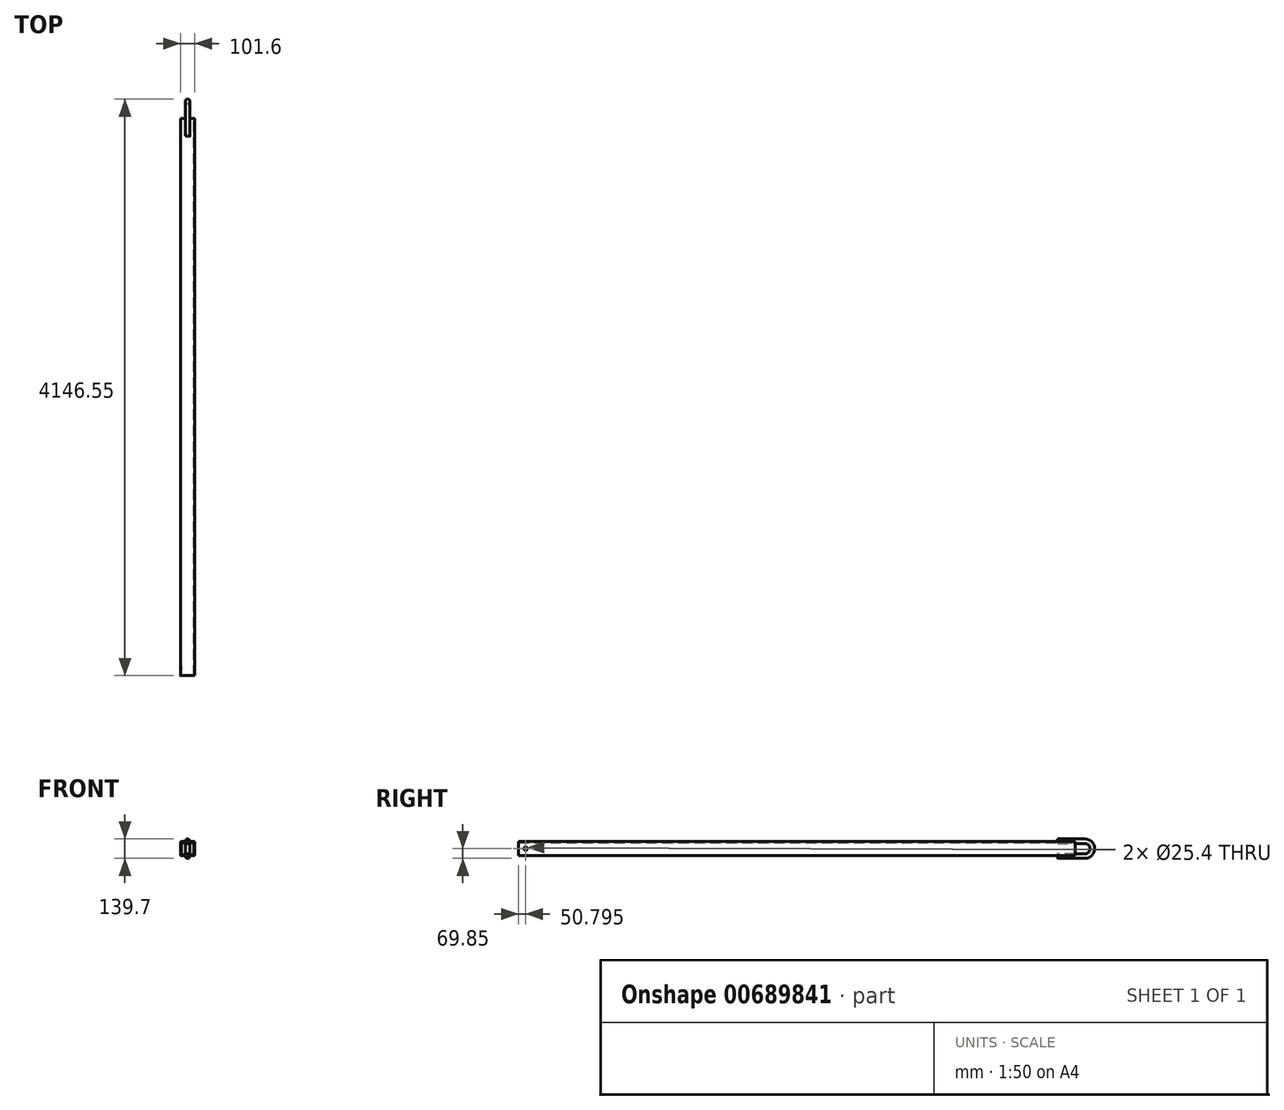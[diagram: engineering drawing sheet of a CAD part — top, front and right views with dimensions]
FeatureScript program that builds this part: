
annotation { "Feature Type Name" : "Feature", "Feature Type Description" : "" }
export const myFeature = defineFeature(function(context is Context, id is Id, definition is map)
    precondition{}
    {
        {
            var Q0;
            Q0=qCreatedBy(makeId("Front.planeOp"),FACE);
            var sketch = newSketch(context, id + "F0", { "sketchPlane" : qUnion([Q0])});
            skLineSegment(sketch, "E0.bottom", {"start": v(-44.07, -44.07) * mm, "end": v(44.07, -44.07) * mm});
            skLineSegment(sketch, "E0.top", {"start": v(-44.07, 44.07) * mm, "end": v(44.07, 44.07) * mm});
            skLineSegment(sketch, "E0.left", {"start": v(-44.07, -44.07) * mm, "end": v(-44.07, 44.07) * mm});
            skLineSegment(sketch, "E0.right", {"start": v(44.07, -44.07) * mm, "end": v(44.07, 44.07) * mm});
            skPoint(sketch, "E0.middle", {"position": v(0, 0) * mm});
            skLineSegment(sketch, "E1.bottom", {"start": v(-50.8, -50.8) * mm, "end": v(50.8, -50.8) * mm});
            skLineSegment(sketch, "E1.top", {"start": v(-50.8, 50.8) * mm, "end": v(50.8, 50.8) * mm});
            skLineSegment(sketch, "E1.left", {"start": v(-50.8, -50.8) * mm, "end": v(-50.8, 50.8) * mm});
            skLineSegment(sketch, "E1.right", {"start": v(50.8, -50.8) * mm, "end": v(50.8, 50.8) * mm});
            skSolve(sketch);
        }
        {
            var Q0;
            Q0 = qSketchRegion(id + "F0", true);
            extrude(context, id + "F1", {"entities" : qUnion([Q0]), "endBound" : BoundingType.SYMMETRIC, "depth" : 4006.85 * mm, "offsetDistance" : 25.4 * mm});
        }
        {
            var Q0;
            Q0=makeQuery(id+"F1.opExtrude","SWEPT_FACE",FACE,{"disambiguationData":[OSD([sQuery(id+"F0.wireOp",EDGE,"E1.right")])]});
            var sketch = newSketch(context, id + "F2", { "sketchPlane" : qUnion([Q0])});
            skCircle(sketch, "E2", {"center": v(-1952.62, 0) * mm, "radius": 12.7 * mm});
            skSolve(sketch);
        }
        {
            var Q0;
            Q0 = qSketchRegion(id + "F2", true);
            extrude(context, id + "F3", {"entities" : qUnion([Q0]), "operationType" : NewBodyOperationType.REMOVE, "endBound" : BoundingType.THROUGH_ALL, "oppositeDirection" : true, "depth" : 25.4 * mm, "offsetDistance" : 25.4 * mm});
        }
        {
            var Q0;
            Q0=qCreatedBy(makeId("Right.planeOp"),FACE);
            var sketch = newSketch(context, id + "F4", { "sketchPlane" : qUnion([Q0])});
            skLineSegment(sketch, "E3.bottom", {"start": v(1876.42, 53.34) * mm, "end": v(2073.28, 53.34) * mm});
            skLineSegment(sketch, "E3.top", {"start": v(1876.42, -53.34) * mm, "end": v(2073.28, -53.34) * mm});
            skLineSegment(sketch, "E3.left", {"start": v(1876.42, 53.34) * mm, "end": v(1876.42, -53.34) * mm, "construction": true});
            skLineSegment(sketch, "E4", {"start": v(1876.42, 0) * mm, "end": v(2004.35, 0) * mm, "construction": true});
            skArc(sketch, "E5", {"start": v(2073.28, -53.34) * mm, "mid": v(2126.62, 0) * mm, "end": v(2073.28, 53.34) * mm});
            skSolve(sketch);
        }
        {
            var Q0;
            Q0=sQuery(id+"F4.wireOp",VERTEX,"E3.bottom.start");
            var Q1;
            Q1=qCreatedBy(makeId("Front.planeOp"),FACE);
            cPlane(context, id + "F5", {"entities" : qUnion([Q0, Q1]), "cplaneType" : CPlaneType.PLANE_POINT, "offset" : 25.4 * mm, "width" : 152.4 * mm, "height" : 152.4 * mm});
        }
        {
            var Q0;
            Q0=qCreatedBy(id+"F5.planeOp",FACE);
            var sketch = newSketch(context, id + "F6", { "sketchPlane" : qUnion([Q0])});
            skPoint(sketch, "E6.0", {"position": v(0, 53.34) * mm});
            skCircle(sketch, "E7", {"center": v(0, 53.34) * mm, "radius": 16.51 * mm});
            skSolve(sketch);
        }
        {
            var Q0;
            Q0=makeQuery(id+"F6.imprint","IMPRINT",FACE,{"disambiguationData":[TD([[makeQuery(id+"F6.imprint","IMPRINT",EDGE,{"derivedFrom":sQuery(id+"F6.wireOp",EDGE,"E7")}),1.0]])]});
            var Q1;
            Q1 = qConstructionFilter(qBodyType(qCreatedBy(id + "F4" ,EDGE), BodyType.WIRE), ConstructionObject.NO);
            sweep(context, id + "F7", {"operationType" : NewBodyOperationType.ADD, "profiles" : qUnion([Q0]), "path" : qUnion([Q1])});
        }
        {
            var Q0;
            Q0=makeQuery(id+"F1.opExtrude","SWEPT_EDGE",EDGE,{"disambiguationData":[OSD([sQuery(id+"F0.wireOp",EDGE,"E1.top"),sQuery(id+"F0.wireOp",EDGE,"E1.right")])]});
            var Q1;
            Q1=makeQuery(id+"F1.opExtrude","SWEPT_EDGE",EDGE,{"disambiguationData":[OSD([sQuery(id+"F0.wireOp",EDGE,"E1.top"),sQuery(id+"F0.wireOp",EDGE,"E1.left")])]});
            var Q2;
            Q2=makeQuery(id+"F1.opExtrude","SWEPT_EDGE",EDGE,{"disambiguationData":[OSD([sQuery(id+"F0.wireOp",EDGE,"E1.bottom"),sQuery(id+"F0.wireOp",EDGE,"E1.right")])]});
            var Q3;
            Q3=makeQuery(id+"F1.opExtrude","SWEPT_EDGE",EDGE,{"disambiguationData":[OSD([sQuery(id+"F0.wireOp",EDGE,"E1.bottom"),sQuery(id+"F0.wireOp",EDGE,"E1.left")])]});
            fillet(context, id + "F8", {"entities" : qUnion([Q0, Q1, Q2, Q3]), "tangentPropagation" : true, "radius" : 5.08 * mm, "defaultsChanged" : false, "vertexSettings" : [], "allowEdgeOverflow" : false});
        }
    });
